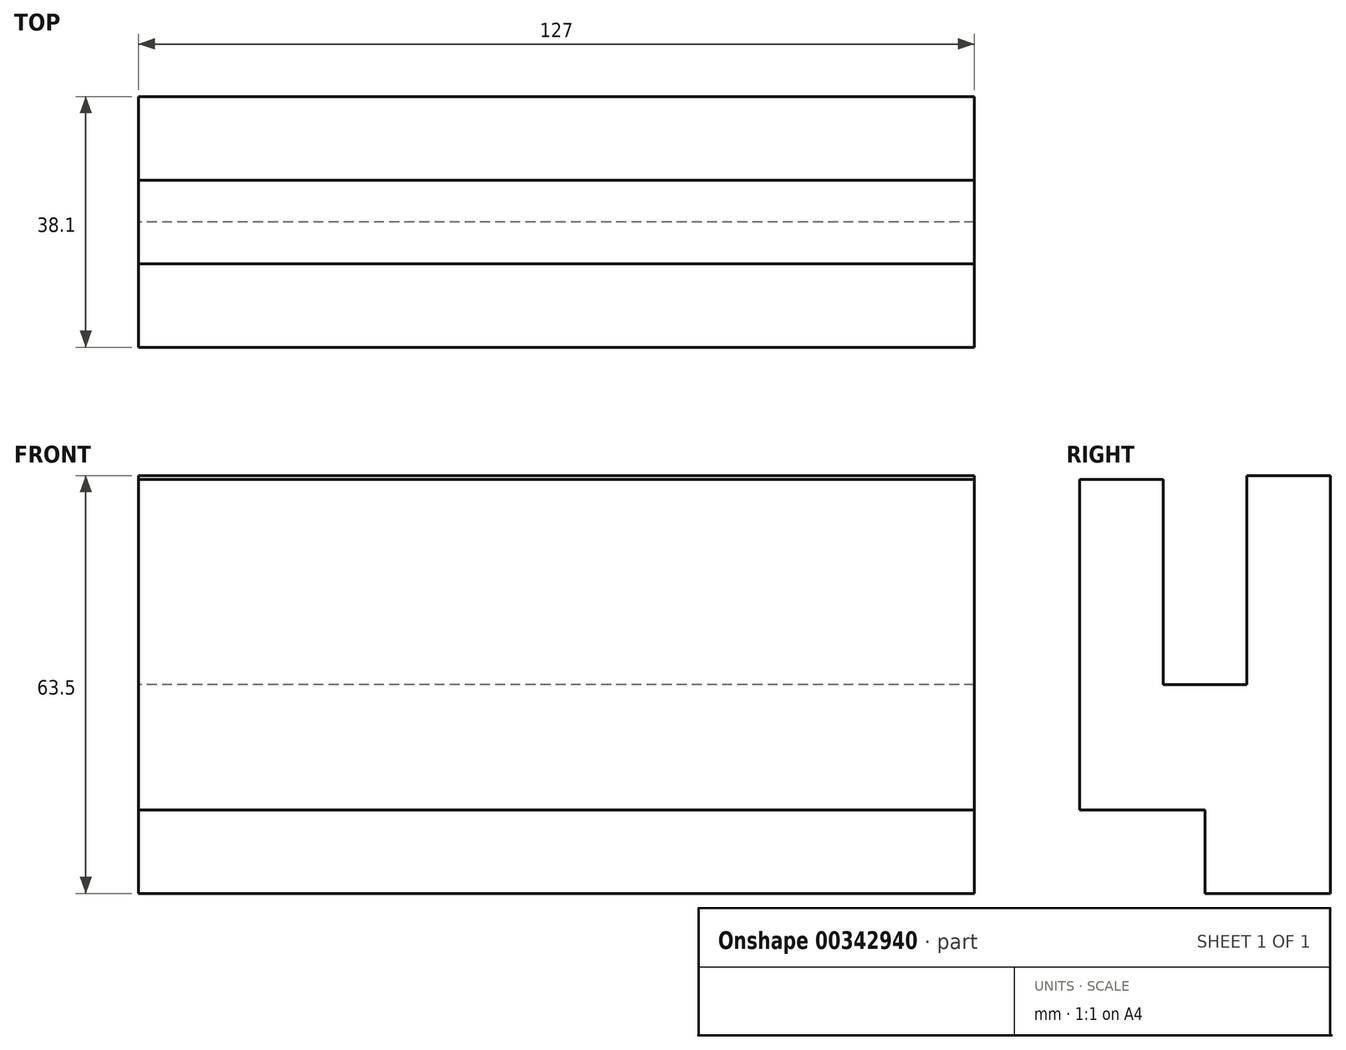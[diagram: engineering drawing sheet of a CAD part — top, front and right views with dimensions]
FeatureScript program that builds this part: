
annotation { "Feature Type Name" : "Feature", "Feature Type Description" : "" }
export const myFeature = defineFeature(function(context is Context, id is Id, definition is map)
    precondition{}
    {
        {
            var Q0;
            Q0=qCreatedBy(makeId("Right.planeOp"),FACE);
            var sketch = newSketch(context, id + "F0", { "sketchPlane" : qUnion([Q0])});
            skLineSegment(sketch, "E0", {"start": v(-51.4, 30.92) * mm, "end": v(-51.4, -19.88) * mm});
            skLineSegment(sketch, "E1", {"start": v(-51.4, -19.88) * mm, "end": v(-32.35, -19.88) * mm});
            skLineSegment(sketch, "E2", {"start": v(-32.35, -19.88) * mm, "end": v(-32.35, -32.58) * mm});
            skLineSegment(sketch, "E3", {"start": v(-32.35, -32.58) * mm, "end": v(-13.3, -32.58) * mm});
            skLineSegment(sketch, "E4", {"start": v(-13.3, -32.58) * mm, "end": v(-13.3, 30.92) * mm});
            skLineSegment(sketch, "E5", {"start": v(-13.3, 30.92) * mm, "end": v(-26, 30.92) * mm});
            skLineSegment(sketch, "E6", {"start": v(-26, 30.92) * mm, "end": v(-26, -0.83) * mm});
            skLineSegment(sketch, "E7", {"start": v(-26, -0.83) * mm, "end": v(-38.7, -0.83) * mm});
            skLineSegment(sketch, "E8", {"start": v(-38.7, -0.83) * mm, "end": v(-38.7, 30.35) * mm});
            skLineSegment(sketch, "E9", {"start": v(-38.7, 30.35) * mm, "end": v(-51.4, 30.35) * mm});
            skSolve(sketch);
        }
        {
            var Q0;
            Q0 = qSketchRegion(id + "F0", true);
            extrude(context, id + "F1", {"entities" : qUnion([Q0]), "depth" : 127 * mm});
        }
    });
